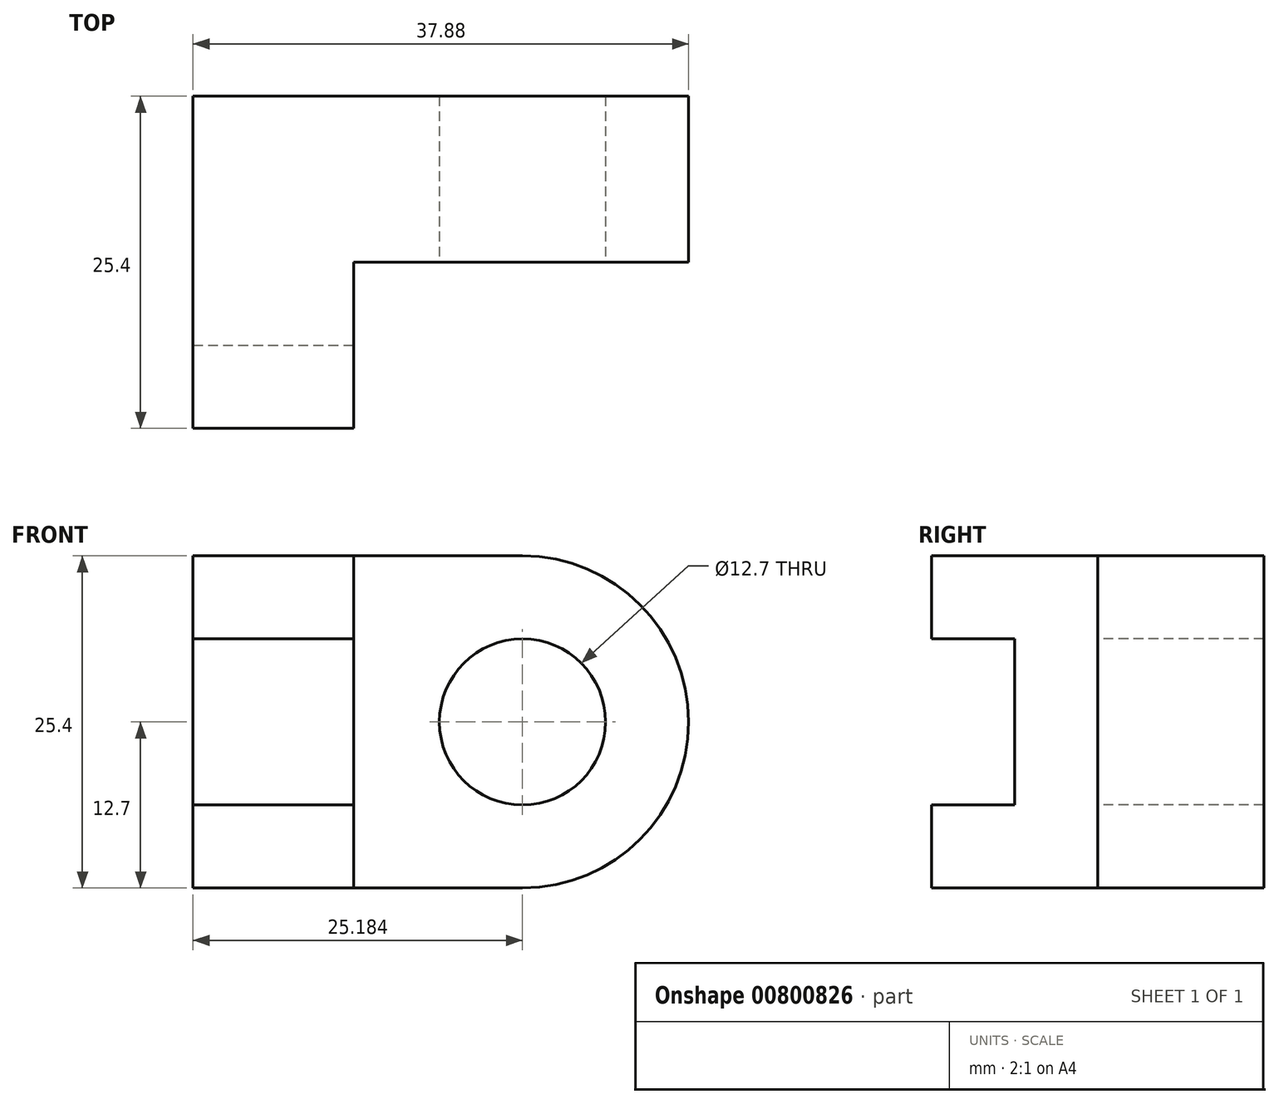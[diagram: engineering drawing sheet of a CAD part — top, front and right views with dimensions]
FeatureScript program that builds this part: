
annotation { "Feature Type Name" : "Feature", "Feature Type Description" : "" }
export const myFeature = defineFeature(function(context is Context, id is Id, definition is map)
    precondition{}
    {
        {
            var Q0;
            Q0=qCreatedBy(makeId("Front.planeOp"),FACE);
            var sketch = newSketch(context, id + "F0", { "sketchPlane" : qUnion([Q0])});
            skLineSegment(sketch, "E0", {"start": v(0, 0) * mm, "end": v(0, 25.4) * mm});
            skLineSegment(sketch, "E1", {"start": v(0, 0) * mm, "end": v(38.1, 0) * mm});
            skLineSegment(sketch, "E2", {"start": v(38.1, 0) * mm, "end": v(38.1, 25.4) * mm});
            skLineSegment(sketch, "E3", {"start": v(0, 25.4) * mm, "end": v(38.1, 25.4) * mm});
            skLineSegment(sketch, "E4", {"start": v(0, 25.4) * mm, "end": v(12.7, 25.4) * mm});
            skSolve(sketch);
        }
        {
            var Q0;
            Q0=makeQuery(id+"F0.imprint","IMPRINT",FACE,{"disambiguationData":[TD([[makeQuery(id+"F0.imprint","IMPRINT",EDGE,{"derivedFrom":sQuery(id+"F0.wireOp",EDGE,"E0")}),-1.0]])]});
            extrude(context, id + "F1", {"entities" : qUnion([Q0]), "depth" : 25.4 * mm, "offsetDistance" : 25.4 * mm});
        }
        {
            var Q0;
            Q0=makeQuery(id+"F1.opExtrude","SWEPT_FACE",FACE,{"disambiguationData":[OSD([sQuery(id+"F0.wireOp",EDGE,"E3"),sQuery(id+"F0.wireOp",EDGE,"E4")])]});
            var sketch = newSketch(context, id + "F2", { "sketchPlane" : qUnion([Q0])});
            skLineSegment(sketch, "E5", {"start": v(12.27, -25.4) * mm, "end": v(12.27, -12.7) * mm});
            skLineSegment(sketch, "E6", {"start": v(12.27, -12.7) * mm, "end": v(38.1, -12.7) * mm});
            skSolve(sketch);
        }
        {
            var Q0;
            {var subQ0=sQuery(id+"F2.wireOp",EDGE,"E5");Q0=makeQuery(id+"F2.imprint","IMPRINT",FACE,{"disambiguationData":[TD([[makeQuery(id+"F2.imprint","IMPRINT",EDGE,{"derivedFrom":subQ0}),-1.0]])]});}
            extrude(context, id + "F3", {"entities" : qUnion([Q0]), "operationType" : NewBodyOperationType.REMOVE, "oppositeDirection" : true, "depth" : 25.4 * mm, "offsetDistance" : 25.4 * mm});
        }
        {
            var Q0;
            Q0=makeQuery(id+"F3.boolean.opBoolean","COPY",FACE,{"derivedFrom":makeQuery(id+"F3.opExtrude","SWEPT_FACE",FACE,{"disambiguationData":[OSD([sQuery(id+"F2.wireOp",EDGE,"E6")])]})});
            var sketch = newSketch(context, id + "F4", { "sketchPlane" : qUnion([Q0])});
            skLineSegment(sketch, "E7", {"start": v(12.27, 25.4) * mm, "end": v(25.18, 25.4) * mm});
            skLineSegment(sketch, "E8", {"start": v(25.18, 25.4) * mm, "end": v(25.18, 0) * mm});
            skArc(sketch, "E9", {"start": v(25.18, 0) * mm, "mid": v(37.88, 12.7) * mm, "end": v(25.18, 25.4) * mm});
            skSolve(sketch);
        }
        {
            var Q0;
            {var subQ0=sQuery(id+"F4.wireOp",EDGE,"E9");Q0=makeQuery(id+"F4.imprint","IMPRINT",FACE,{"disambiguationData":[TD([[makeQuery(id+"F4.imprint","IMPRINT",EDGE,{"derivedFrom":subQ0}),-1.0]])]});}
            extrude(context, id + "F5", {"entities" : qUnion([Q0]), "operationType" : NewBodyOperationType.REMOVE, "oppositeDirection" : true, "depth" : 25.4 * mm, "offsetDistance" : 25.4 * mm});
        }
        {
            var Q0;
            Q0=makeQuery(id+"F3.boolean.opBoolean","COPY",FACE,{"derivedFrom":makeQuery(id+"F3.opExtrude","SWEPT_FACE",FACE,{"disambiguationData":[OSD([sQuery(id+"F2.wireOp",EDGE,"E5")])]})});
            var sketch = newSketch(context, id + "F6", { "sketchPlane" : qUnion([Q0])});
            skLineSegment(sketch, "E10", {"start": v(-25.4, 25.4) * mm, "end": v(-25.4, 19.05) * mm});
            skLineSegment(sketch, "E11", {"start": v(-25.4, 19.05) * mm, "end": v(-19.05, 19.05) * mm});
            skLineSegment(sketch, "E12", {"start": v(-19.05, 19.05) * mm, "end": v(-19.05, 6.35) * mm});
            skLineSegment(sketch, "E13", {"start": v(-19.05, 6.35) * mm, "end": v(-25.4, 6.35) * mm});
            skSolve(sketch);
        }
        {
            var Q0;
            {var subQ0=sQuery(id+"F6.wireOp",EDGE,"E11");Q0=makeQuery(id+"F6.imprint","IMPRINT",FACE,{"disambiguationData":[TD([[makeQuery(id+"F6.imprint","IMPRINT",EDGE,{"derivedFrom":subQ0}),-1.0]])]});}
            extrude(context, id + "F7", {"entities" : qUnion([Q0]), "operationType" : NewBodyOperationType.REMOVE, "oppositeDirection" : true, "depth" : 25.4 * mm, "offsetDistance" : 25.4 * mm});
        }
        {
            var Q0;
            Q0=makeQuery(id+"F3.boolean.opBoolean","COPY",FACE,{"derivedFrom":makeQuery(id+"F3.opExtrude","SWEPT_FACE",FACE,{"disambiguationData":[OSD([sQuery(id+"F2.wireOp",EDGE,"E6")])]})});
            var sketch = newSketch(context, id + "F8", { "sketchPlane" : qUnion([Q0])});
            skLineSegment(sketch, "E14", {"start": v(25.18, 25.4) * mm, "end": v(25.18, 0) * mm, "construction": true});
            skLineSegment(sketch, "E15", {"start": v(25.18, 0) * mm, "end": v(37.88, 12.7) * mm, "construction": true});
            skLineSegment(sketch, "E16", {"start": v(37.88, 12.7) * mm, "end": v(31.53, 12.7) * mm, "construction": true});
            skCircle(sketch, "E17", {"center": v(25.18, 12.7) * mm, "radius": 6.35 * mm});
            skSolve(sketch);
        }
        {
            var Q0;
            Q0=makeQuery(id+"F8.imprint","IMPRINT",FACE,{"disambiguationData":[TD([[makeQuery(id+"F8.imprint","IMPRINT",EDGE,{"derivedFrom":sQuery(id+"F8.wireOp",EDGE,"E17")}),1.0]])]});
            extrude(context, id + "F9", {"entities" : qUnion([Q0]), "operationType" : NewBodyOperationType.REMOVE, "oppositeDirection" : true, "depth" : 25.4 * mm, "offsetDistance" : 25.4 * mm});
        }
    });
